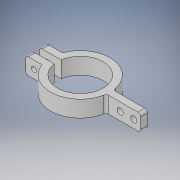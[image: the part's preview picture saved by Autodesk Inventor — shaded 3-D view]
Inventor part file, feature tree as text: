
AUTODESK INVENTOR PART (.ipt)
format: ipt  version: 2019 (Build 230136000, 136)  size: 179,712 bytes
history: native  units: in
note: dims shown in document units (in); Inventor stores cm internally (conversion verified against a paired STEP export)
features: sketch x5, hole x3, extrude x2, fillet x2, plane x1
ambient origin geometry x8: Origin, YZ Plane, XZ Plane, XY Plane, X Axis, Y Axis, Z Axis, Center Point
bodies: Solid1 (feature_tree)
feature tree (13):
  extrude  "Extrusion1"  Depth=0.1969in
  hole  "Hole1"  [1 undecoded]
  extrude  "Extrusion2"  Depth=0.4724in
  plane  "Work Plane3"
  hole  "Hole3"  [1 undecoded]
  hole  "Hole4"  [1 undecoded]
  fillet  "Fillet2"  Radius=0.7776in
  fillet  "Fillet3"  Radius=0.1969in
  sketch  "Sketch1"  dims[d0=1.3189in d1=0.1969in]
  sketch  "Sketch2"  dims[d4=0.1969in d5=0.1969in]
  sketch  "Sketch3"  dims[d6=0.3937in d7=0.4724in]
  sketch  "Sketch6"  dims[d8=0.4724in d9=0.0in]
  sketch  "Sketch7"  dims[d10=0.1495in d11=0.2362in d12=0.279in d13=0.0787in d14=0.5635in d15=0.315in d16=0.8108in d17=0.3159in d18=0.106in d19=0.0in d24=0.7776in d35=0.1969in d36=0.9843in d37=0.104in d38=0.276in d39=0.279in d40=0.0787in d41=0.5635in d42=0.4322in d43=0.8108in d44=0.1969in d45=0.3937in d46=0.177in d47=0.12in d48=0.332in d49=0.0787in d50=0.5635in d51=0.315in d52=0.8108in d53=0.0787in d54=0.0787in]
note: 3 required parameter values undecoded (feature->parameter linkage not recoverable at this tier; creation-order binding heuristic only, values carry confidence <= 0.55)
